# Revit family: TD92_VIC270_ROS060_RVT20_R00
name_source: partatom
category: Mobiliário
units: mm (PartAtom-declared; Revit-internal decimal feet)

## family parameters
Com base no plano de trabalho = Não
Compartilhado = Não
Corte com vazios quando carregada = Não
Número OmniClass = 23.40.20.00
Ponto de cálculo do ambiente = Não
Sempre na vertical = Sim
Título OmniClass = General Furniture and Specialties

## types (1)
- TD92_VIC270_ROS060_RVT20_R00
    Descrição = A Cadeira Infantil Tramontina Vice em Polipropileno vai deixar o espaço dos pequenos mais charmoso e cheio de vida. Confortável e com design que preza pelo bem-estar e alegria das crianças, ela agrada também aos pais. Produzida em polipropileno, é totalmente livre de material tóxico. Leve e compacta, é fácil de transportar. As crianças vão amar a novidade!
    Elevação padrão = 0  [stored 0 ft]
    Fabricante = Tramontina Delta S/A
    Modelo = Cadeira Infantil Tramontina Vice em Polipropileno Rosa
    Nota-chave = 92270060
    URL = https://www.tramontinastore.com

note: [stored X ft] marks values corroborated as IEEE doubles in the binary element streams (Revit-internal decimal feet)
